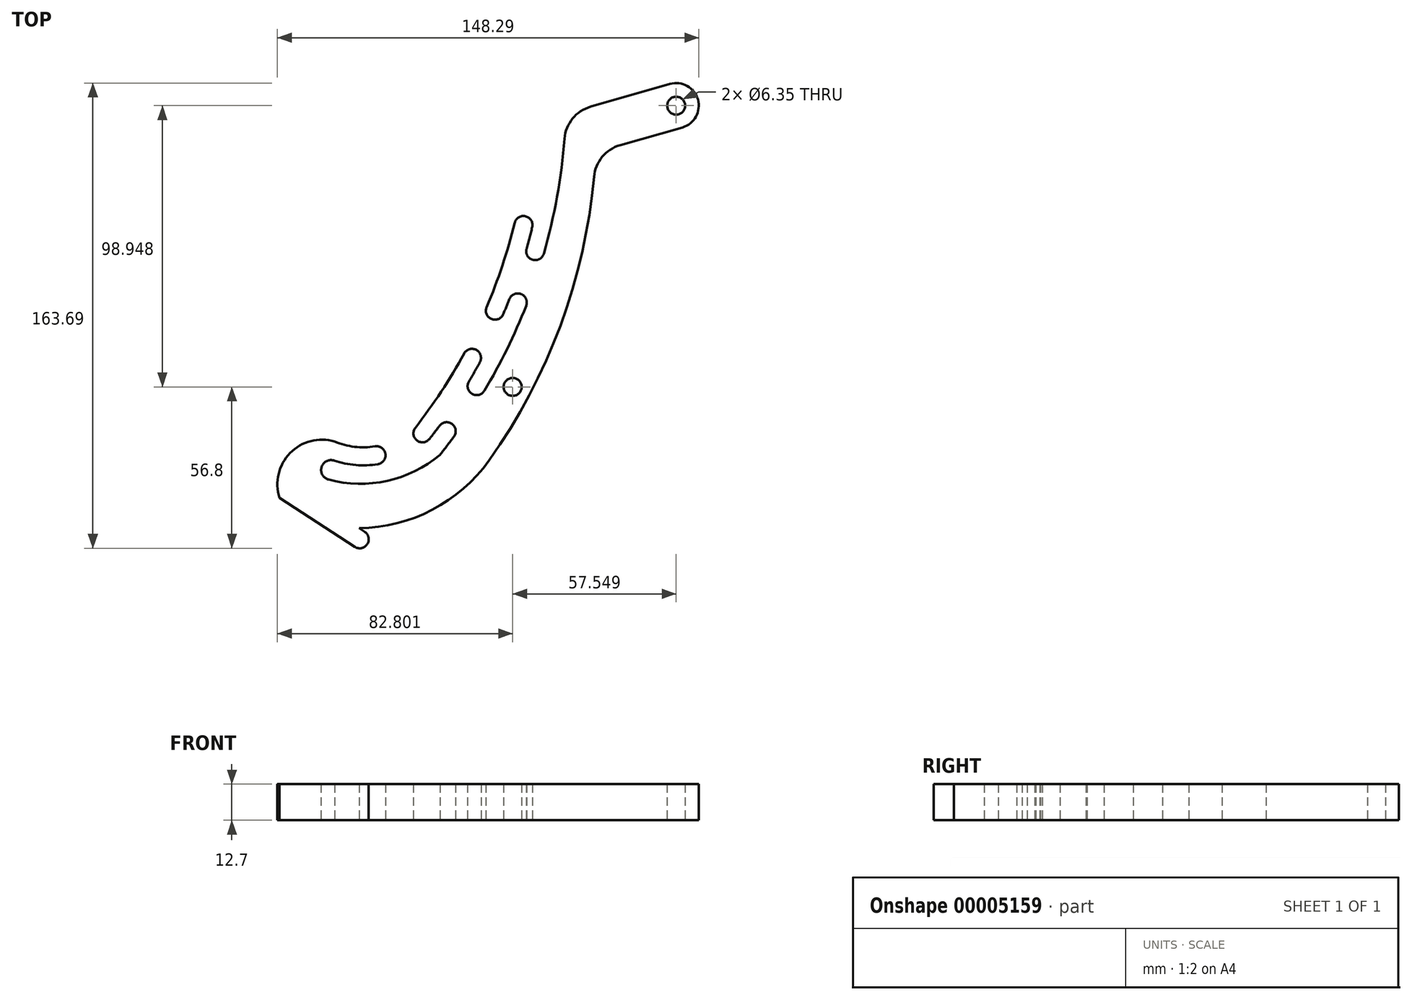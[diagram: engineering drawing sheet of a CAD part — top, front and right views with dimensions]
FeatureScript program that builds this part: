
annotation { "Feature Type Name" : "Feature", "Feature Type Description" : "" }
export const myFeature = defineFeature(function(context is Context, id is Id, definition is map)
    precondition{}
    {
        {
            var Q0;
            Q0=qCreatedBy(makeId("Top.planeOp"),FACE);
            var sketch = newSketch(context, id + "F0", { "sketchPlane" : qUnion([Q0])});
            skCircle(sketch, "E0", {"center": v(38.1, 76.37) * mm, "radius": 7.94 * mm});
            skLineSegment(sketch, "E1", {"start": v(0, 53.27) * mm, "end": v(0, -67.66) * mm, "construction": true});
            skCircle(sketch, "E2", {"center": v(38.1, 76.37) * mm, "radius": 3.18 * mm});
            skLineSegment(sketch, "E3", {"start": v(35.92, 84) * mm, "end": v(-0.71, 73.51) * mm});
            skLineSegment(sketch, "E4", {"start": v(40.28, 68.74) * mm, "end": v(9.76, 60) * mm});
            skArc(sketch, "E5", {"start": v(-27.77, -48.45) * mm, "mid": v(-1.2, 3.07) * mm, "end": v(9.76, 60) * mm});
            skArc(sketch, "E6", {"start": v(-45.04, -46.49) * mm, "mid": v(-13.19, 9.94) * mm, "end": v(-0.71, 73.51) * mm});
            skCircle(sketch, "E7", {"center": v(-15.66, 34.37) * mm, "radius": 3.18 * mm});
            skCircle(sketch, "E8", {"center": v(-25.7, 4.25) * mm, "radius": 3.18 * mm});
            skCircle(sketch, "E9", {"center": v(-69.88, 242.64) * mm, "radius": 7.21 * mm});
            skArc(sketch, "E10.0", {"start": v(-22.78, 3) * mm, "mid": v(-17.05, 18.1) * mm, "end": v(-12.58, 33.62) * mm});
            skArc(sketch, "E11.0", {"start": v(-28.62, 5.5) * mm, "mid": v(-23.07, 20.1) * mm, "end": v(-18.74, 35.12) * mm});
            skCircle(sketch, "E12", {"center": v(-17.65, 7.15) * mm, "radius": 3.17 * mm});
            skCircle(sketch, "E13", {"center": v(-11.53, 25.19) * mm, "radius": 3.17 * mm});
            skCircle(sketch, "E14.1.0", {"center": v(-51.2, -38.9) * mm, "radius": 3.18 * mm});
            skCircle(sketch, "E14.1.1", {"center": v(-33.76, -12.37) * mm, "radius": 3.18 * mm});
            skArc(sketch, "E14.1.2", {"start": v(-53.7, -36.95) * mm, "mid": v(-44.59, -24.25) * mm, "end": v(-36.55, -10.85) * mm});
            skArc(sketch, "E14.1.3", {"start": v(-48.7, -40.86) * mm, "mid": v(-39.28, -27.74) * mm, "end": v(-30.97, -13.9) * mm});
            skCircle(sketch, "E14.1.4", {"center": v(-32.13, -22.3) * mm, "radius": 3.17 * mm});
            skCircle(sketch, "E14.1.5", {"center": v(-42.67, -38.17) * mm, "radius": 3.17 * mm});
            skLineSegment(sketch, "E14.anchor1", {"start": v(-203.8, 80.35) * mm, "end": v(-25.7, 4.25) * mm, "construction": true});
            skArc(sketch, "E15", {"start": v(-97.36, -67.33) * mm, "mid": v(-97.36, -67.33) * mm, "end": v(-97.36, -67.33) * mm});
            skCircle(sketch, "E16", {"center": v(-94.11, -60.1) * mm, "radius": 7.94 * mm, "construction": true});
            skArc(sketch, "E17", {"start": v(-84.28, -55.18) * mm, "mid": v(-63.6, -55.63) * mm, "end": v(-45.04, -46.49) * mm});
            skPoint(sketch, "E18.orphan", {"position": v(-85.08, -71.24) * mm});
            skCircle(sketch, "E19", {"center": v(-19.45, -22.58) * mm, "radius": 3.18 * mm});
            skLineSegment(sketch, "E20", {"start": v(-101.5, -61.66) * mm, "end": v(-75, -78.87) * mm});
            skLineSegment(sketch, "E21", {"start": v(-101.5, -61.66) * mm, "end": v(-94.11, -60.1) * mm, "construction": true});
            skLineSegment(sketch, "E22.0", {"start": v(-92.71, -59.8) * mm, "end": v(-92.71, -59.8) * mm});
            skCircle(sketch, "E23", {"center": v(-73.27, -76.2) * mm, "radius": 3.18 * mm});
            skPoint(sketch, "E24.orphan", {"position": v(-68.48, -71.24) * mm});
            skLineSegment(sketch, "E25", {"start": v(-32.13, -22.3) * mm, "end": v(-54.92, -1.1) * mm, "construction": true});
            skLineSegment(sketch, "E26", {"start": v(-42.67, -38.17) * mm, "end": v(-62.33, -19.9) * mm, "construction": true});
            skArc(sketch, "E27.trimOffspring", {"start": v(-73.45, -72.3) * mm, "mid": v(-47.75, -65.84) * mm, "end": v(-27.77, -48.45) * mm});
            skLineSegment(sketch, "E28.trimOffspring", {"start": v(-73.45, -72.3) * mm, "end": v(-71.55, -73.54) * mm});
            skArc(sketch, "E29.0", {"start": v(-82.28, -48.52) * mm, "mid": v(-66.4, -49.71) * mm, "end": v(-51.9, -43.17) * mm});
            skArc(sketch, "E30.0", {"start": v(-82.1, -41.8) * mm, "mid": v(-68.56, -43.62) * mm, "end": v(-55.97, -38.3) * mm});
            skCircle(sketch, "E31", {"center": v(-67.37, -46.65) * mm, "radius": 3.18 * mm});
            skArc(sketch, "E32", {"start": v(-82.28, -48.52) * mm, "mid": v(-86.72, -50.82) * mm, "end": v(-84.28, -55.18) * mm});
            skArc(sketch, "E33", {"start": v(-82.1, -41.8) * mm, "mid": v(-97.78, -45.88) * mm, "end": v(-101.5, -61.66) * mm});
            skPoint(sketch, "E34.orphan", {"position": v(-88.77, -53.72) * mm});
            skSolve(sketch);
        }
        {
            var Q0;
            {var subQ3=sQuery(id+"F0.wireOp",EDGE,"e6a3bfc2-b61a-4404-be60-c5dfc7bfd3ce");var subQ7=makeQuery(id+"F0.imprint","INTERSECT",VERTEX,{"derivedFrom":[subQ3,sQuery(id+"F0.wireOp",EDGE,"E6")]});Q0=makeQuery(id+"F0.imprint","IMPRINT",FACE,{"disambiguationData":[TD([[makeQuery(id+"F0.imprint","IMPRINT",EDGE,{"disambiguationData":[TD([[subQ7,1.0]])],"derivedFrom":subQ3}),1.0]])]});}
            var Q1;
            Q1=makeQuery(id+"F0.imprint","IMPRINT",FACE,{"disambiguationData":[TD([[makeQuery(id+"F0.imprint","IMPRINT",EDGE,{"derivedFrom":sQuery(id+"F0.wireOp",EDGE,"E2")}),-1.0]])]});
            var Q2;
            {var subQ7=sQuery(id+"F0.wireOp",EDGE,"E3");Q2=makeQuery(id+"F0.imprint","IMPRINT",FACE,{"disambiguationData":[TD([[makeQuery(id+"F0.imprint","IMPRINT",EDGE,{"derivedFrom":subQ7}),1.0]])]});}
            var Q3;
            {var subQ0=sQuery(id+"F0.wireOp",EDGE,"E11.0");Q3=makeQuery(id+"F0.imprint","IMPRINT",FACE,{"disambiguationData":[TD([[makeQuery(id+"F0.imprint","IMPRINT",EDGE,{"derivedFrom":subQ0}),-1.0]])]});}
            var Q4;
            {var subQ0=sQuery(id+"F0.wireOp",EDGE,"E8");var subQ2=makeQuery(id+"F0.imprint","INTERSECT",VERTEX,{"derivedFrom":[subQ0,sQuery(id+"F0.wireOp",EDGE,"E10.0")]});Q4=makeQuery(id+"F0.imprint","IMPRINT",FACE,{"disambiguationData":[TD([[makeQuery(id+"F0.imprint","IMPRINT",EDGE,{"disambiguationData":[TD([[subQ2,1.0]])],"derivedFrom":subQ0}),1.0]])]});}
            var Q5;
            {var subQ0=sQuery(id+"F0.wireOp",EDGE,"E7");var subQ2=makeQuery(id+"F0.imprint","INTERSECT",VERTEX,{"derivedFrom":[subQ0,sQuery(id+"F0.wireOp",EDGE,"E10.0")]});Q5=makeQuery(id+"F0.imprint","IMPRINT",FACE,{"disambiguationData":[TD([[makeQuery(id+"F0.imprint","IMPRINT",EDGE,{"disambiguationData":[TD([[subQ2,1.0]])],"derivedFrom":subQ0}),1.0]])]});}
            var Q6;
            {var subQ3=sQuery(id+"F0.wireOp",EDGE,"E6");var subQ5=sQuery(id+"F0.wireOp",EDGE,"E12");var subQ7=makeQuery(id+"F0.imprint","INTERSECT",VERTEX,{"derivedFrom":[subQ3,subQ5]});Q6=makeQuery(id+"F0.imprint","IMPRINT",FACE,{"disambiguationData":[TD([[makeQuery(id+"F0.imprint","IMPRINT",EDGE,{"disambiguationData":[TD([[subQ7,-1.0]])],"derivedFrom":subQ3}),1.0]])]});}
            var Q7;
            {var subQ0=sQuery(id+"F0.wireOp",EDGE,"E14.1.5");var subQ3=sQuery(id+"F0.wireOp",EDGE,"E6");var subQ4=makeQuery(id+"F0.imprint","INTERSECT",VERTEX,{"derivedFrom":[subQ3,subQ0]});Q7=makeQuery(id+"F0.imprint","IMPRINT",FACE,{"disambiguationData":[TD([[makeQuery(id+"F0.imprint","IMPRINT",EDGE,{"disambiguationData":[TD([[subQ4,-1.0]])],"derivedFrom":subQ3}),1.0]])]});}
            var Q8;
            {var subQ7=sQuery(id+"F0.wireOp",EDGE,"E14.1.2");Q8=makeQuery(id+"F0.imprint","IMPRINT",FACE,{"disambiguationData":[TD([[makeQuery(id+"F0.imprint","IMPRINT",EDGE,{"derivedFrom":subQ7}),-1.0]])]});}
            var Q9;
            {var subQ0=sQuery(id+"F0.wireOp",EDGE,"E14.1.1");var subQ2=makeQuery(id+"F0.imprint","INTERSECT",VERTEX,{"derivedFrom":[subQ0,sQuery(id+"F0.wireOp",EDGE,"E14.1.2")]});Q9=makeQuery(id+"F0.imprint","IMPRINT",FACE,{"disambiguationData":[TD([[makeQuery(id+"F0.imprint","IMPRINT",EDGE,{"disambiguationData":[TD([[subQ2,1.0]])],"derivedFrom":subQ0}),1.0]])]});}
            var Q10;
            {var subQ0=sQuery(id+"F0.wireOp",EDGE,"E14.1.0");var subQ2=makeQuery(id+"F0.imprint","INTERSECT",VERTEX,{"derivedFrom":[subQ0,sQuery(id+"F0.wireOp",EDGE,"E14.1.2")]});Q10=makeQuery(id+"F0.imprint","IMPRINT",FACE,{"disambiguationData":[TD([[makeQuery(id+"F0.imprint","IMPRINT",EDGE,{"disambiguationData":[TD([[subQ2,-1.0]])],"derivedFrom":subQ0}),1.0]])]});}
            var Q11;
            Q11=makeQuery(id+"F0.imprint","IMPRINT",FACE,{"disambiguationData":[TD([[makeQuery(id+"F0.imprint","IMPRINT",EDGE,{"derivedFrom":sQuery(id+"F0.wireOp",EDGE,"E16")}),1.0]])]});
            var Q12;
            {var subQ1=sQuery(id+"F0.wireOp",EDGE,"E17");Q12=makeQuery(id+"F0.imprint","IMPRINT",FACE,{"disambiguationData":[TD([[makeQuery(id+"F0.imprint","IMPRINT",EDGE,{"derivedFrom":subQ1}),-1.0]])]});}
            var Q13;
            {var subQ0=sQuery(id+"F0.wireOp",EDGE,"E15");var subQ1=sQuery(id+"F0.wireOp",EDGE,"0dc1026c-85b6-4418-b667-44285368c718");var subQ3=makeQuery(id+"F0.imprint","INTERSECT",VERTEX,{"disambiguationData":[OD(0.0)],"derivedFrom":[subQ1,subQ0]});Q13=makeQuery(id+"F0.imprint","IMPRINT",FACE,{"disambiguationData":[TD([[makeQuery(id+"F0.imprint","IMPRINT",EDGE,{"disambiguationData":[TD([[subQ3,1.0]])],"derivedFrom":subQ1}),1.0]])]});}
            var Q14;
            {var subQ10=sQuery(id+"F0.wireOp",EDGE,"e72493c6-7b6d-4d67-9688-eb90b90bec92");Q14=makeQuery(id+"F0.imprint","IMPRINT",FACE,{"disambiguationData":[TD([[makeQuery(id+"F0.imprint","IMPRINT",EDGE,{"derivedFrom":subQ10}),-1.0]])]});}
            var Q15;
            {var subQ0=sQuery(id+"F0.wireOp",EDGE,"8907a17e-fed9-4a74-8d90-c090a8a5db59");var subQ2=makeQuery(id+"F0.imprint","INTERSECT",VERTEX,{"derivedFrom":[sQuery(id+"F0.wireOp",EDGE,"e72493c6-7b6d-4d67-9688-eb90b90bec92"),subQ0]});Q15=makeQuery(id+"F0.imprint","IMPRINT",FACE,{"disambiguationData":[TD([[makeQuery(id+"F0.imprint","IMPRINT",EDGE,{"disambiguationData":[TD([[subQ2,-1.0]])],"derivedFrom":subQ0}),1.0]])]});}
            var Q16;
            {var subQ0=sQuery(id+"F0.wireOp",EDGE,"E23");var subQ2=makeQuery(id+"F0.imprint","INTERSECT",VERTEX,{"derivedFrom":[sQuery(id+"F0.wireOp",EDGE,"E20"),subQ0]});Q16=makeQuery(id+"F0.imprint","IMPRINT",FACE,{"disambiguationData":[TD([[makeQuery(id+"F0.imprint","IMPRINT",EDGE,{"disambiguationData":[TD([[subQ2,1.0]])],"derivedFrom":subQ0}),1.0]])]});}
            var Q17;
            {var subQ0=sQuery(id+"F0.wireOp",EDGE,"d9d6a084-7d00-465c-bf04-5b505379d810");var subQ1=sQuery(id+"F0.wireOp",EDGE,"E15");var subQ2=makeQuery(id+"F0.imprint","INTERSECT",VERTEX,{"derivedFrom":[subQ1,subQ0]});Q17=makeQuery(id+"F0.imprint","IMPRINT",FACE,{"disambiguationData":[TD([[makeQuery(id+"F0.imprint","IMPRINT",EDGE,{"disambiguationData":[TD([[subQ2,1.0]])],"derivedFrom":subQ1}),-1.0]])]});}
            var Q18;
            {var subQ0=sQuery(id+"F0.wireOp",EDGE,"E31");var subQ2=makeQuery(id+"F0.imprint","INTERSECT",VERTEX,{"derivedFrom":[sQuery(id+"F0.wireOp",EDGE,"E29.0"),subQ0]});Q18=makeQuery(id+"F0.imprint","IMPRINT",FACE,{"disambiguationData":[TD([[makeQuery(id+"F0.imprint","IMPRINT",EDGE,{"disambiguationData":[TD([[subQ2,1.0]])],"derivedFrom":subQ0}),1.0]])]});}
            extrude(context, id + "F1", {"entities" : qUnion([Q0, Q1, Q2, Q3, Q4, Q5, Q6, Q7, Q8, Q9, Q10, Q11, Q12, Q13, Q14, Q15, Q16, Q17, Q18]), "endBound" : BoundingType.SYMMETRIC, "depth" : 12.7 * mm});
        }
        {
            var Q0;
            Q0=makeQuery(id+"F1.opExtrude","SWEPT_EDGE",EDGE,{"disambiguationData":[OSD([sQuery(id+"F0.wireOp",EDGE,"E3"),sQuery(id+"F0.wireOp",EDGE,"E6")])]});
            fillet(context, id + "F2", {"entities" : qUnion([Q0]), "radius" : 12.7 * mm, "tangentPropagation" : true, "allowEdgeOverflow" : false});
        }
        {
            var Q0;
            Q0=makeQuery(id+"F1.opExtrude","SWEPT_EDGE",EDGE,{"disambiguationData":[OSD([sQuery(id+"F0.wireOp",EDGE,"E4"),sQuery(id+"F0.wireOp",EDGE,"E5")])]});
            fillet(context, id + "F3", {"entities" : qUnion([Q0]), "radius" : 12.7 * mm, "tangentPropagation" : true, "allowEdgeOverflow" : false});
        }
    });
